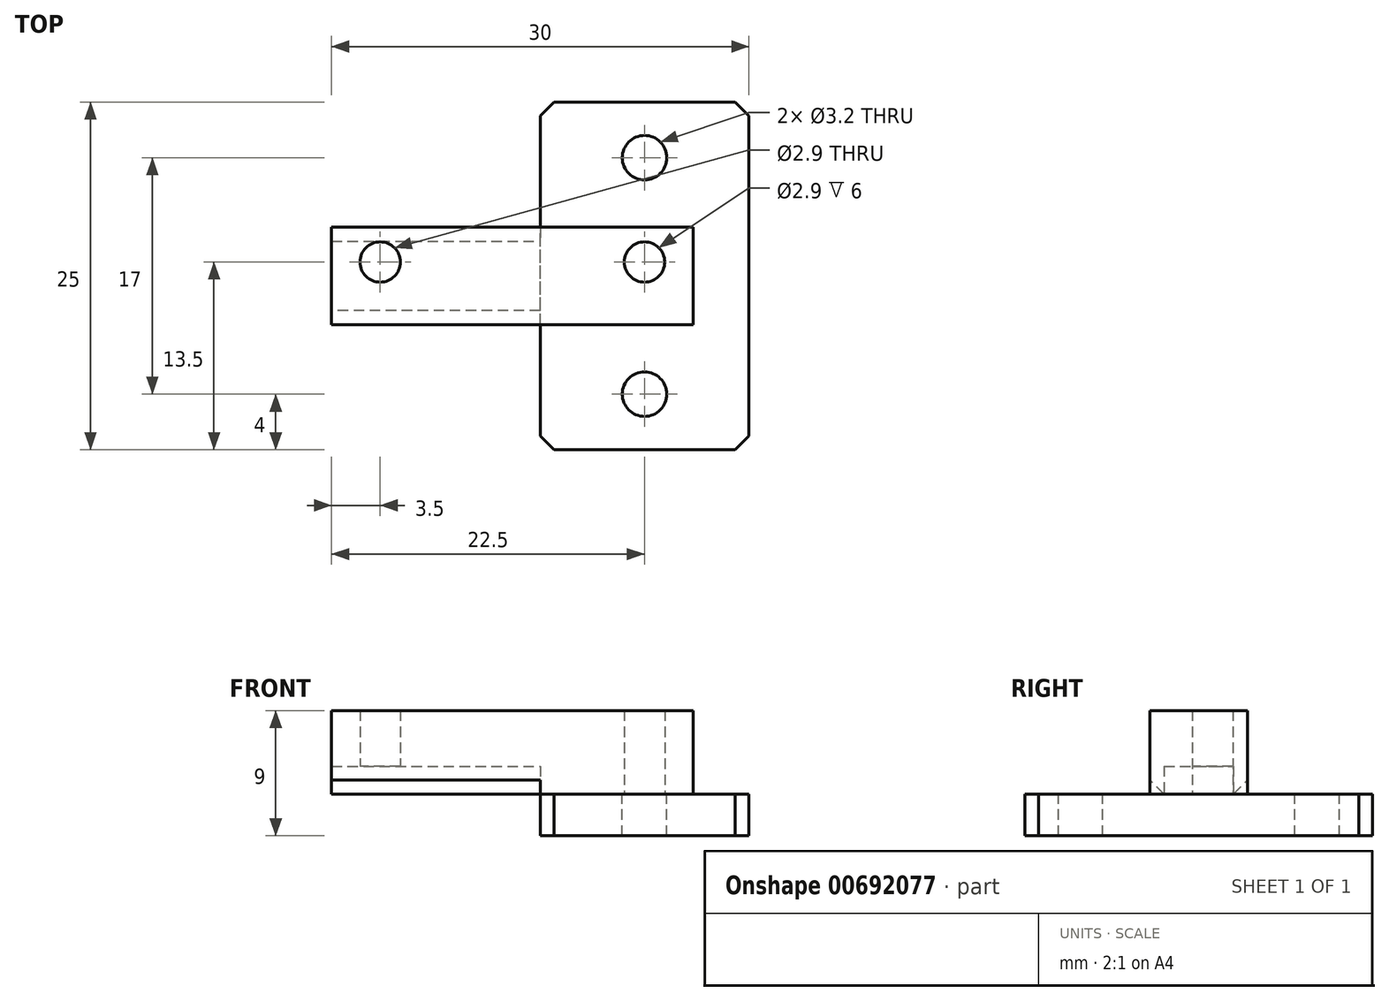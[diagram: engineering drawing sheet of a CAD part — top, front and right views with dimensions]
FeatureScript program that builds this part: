
annotation { "Feature Type Name" : "Feature", "Feature Type Description" : "" }
export const myFeature = defineFeature(function(context is Context, id is Id, definition is map)
    precondition{}
    {
        {
            var Q0;
            Q0=qCreatedBy(makeId("Top.planeOp"),FACE);
            var sketch = newSketch(context, id + "F0", { "sketchPlane" : qUnion([Q0])});
            skLineSegment(sketch, "E0.bottom", {"start": v(0, 0) * mm, "end": v(-26, 0) * mm});
            skLineSegment(sketch, "E0.top", {"start": v(0, 7) * mm, "end": v(-26, 7) * mm});
            skLineSegment(sketch, "E0.left", {"start": v(0, 0) * mm, "end": v(0, 7) * mm});
            skLineSegment(sketch, "E0.right", {"start": v(-26, 0) * mm, "end": v(-26, 7) * mm});
            skCircle(sketch, "E1", {"center": v(-22.5, 4.5) * mm, "radius": 1.45 * mm});
            skCircle(sketch, "E2", {"center": v(-3.5, 4.5) * mm, "radius": 1.45 * mm});
            skSolve(sketch);
        }
        {
            var Q0;
            Q0=makeQuery(id+"F0.imprint","IMPRINT",FACE,{"disambiguationData":[TD([[makeQuery(id+"F0.imprint","IMPRINT",EDGE,{"derivedFrom":sQuery(id+"F0.wireOp",EDGE,"E0.bottom")}),-1.0]])]});
            extrude(context, id + "F1", {"entities" : qUnion([Q0]), "depth" : 6 * mm, "offsetDistance" : 25 * mm});
        }
        {
            var Q0;
            Q0=qCreatedBy(makeId("Top.planeOp"),FACE);
            var sketch = newSketch(context, id + "F2", { "sketchPlane" : qUnion([Q0])});
            skLineSegment(sketch, "E3.bottom", {"start": v(4, -9) * mm, "end": v(-11, -9) * mm});
            skLineSegment(sketch, "E3.top", {"start": v(4, 16) * mm, "end": v(-11, 16) * mm});
            skLineSegment(sketch, "E3.left", {"start": v(4, -9) * mm, "end": v(4, 16) * mm});
            skLineSegment(sketch, "E3.right", {"start": v(-11, -9) * mm, "end": v(-11, 16) * mm});
            skCircle(sketch, "E4", {"center": v(-3.5, -5) * mm, "radius": 1.6 * mm});
            skCircle(sketch, "E5", {"center": v(-3.5, 12) * mm, "radius": 1.6 * mm});
            skLineSegment(sketch, "E6.bottom", {"start": v(-6, -9) * mm, "end": v(-1, -9) * mm});
            skLineSegment(sketch, "E6.top", {"start": v(-6, 16) * mm, "end": v(-1, 16) * mm});
            skLineSegment(sketch, "E6.left", {"start": v(-6, -9) * mm, "end": v(-6, 16) * mm});
            skLineSegment(sketch, "E6.right", {"start": v(-1, -9) * mm, "end": v(-1, 16) * mm});
            skSolve(sketch);
        }
        {
            var Q0;
            Q0 = qSketchRegion(id + "F2", true);
            extrude(context, id + "F3", {"entities" : qUnion([Q0]), "operationType" : NewBodyOperationType.ADD, "oppositeDirection" : true, "depth" : 3 * mm, "offsetDistance" : 25 * mm});
        }
        {
            var Q0;
            Q0=makeQuery(id+"F3.opExtrude","SWEPT_EDGE",EDGE,{"disambiguationData":[OSD([sQuery(id+"F2.wireOp",EDGE,"E3.top"),sQuery(id+"F2.wireOp",EDGE,"E3.left")])]});
            var Q1;
            Q1=makeQuery(id+"F3.opExtrude","SWEPT_EDGE",EDGE,{"disambiguationData":[OSD([sQuery(id+"F2.wireOp",EDGE,"E3.top"),sQuery(id+"F2.wireOp",EDGE,"E3.right")])]});
            var Q2;
            Q2=makeQuery(id+"F3.opExtrude","SWEPT_EDGE",EDGE,{"disambiguationData":[OSD([sQuery(id+"F2.wireOp",EDGE,"E3.bottom"),sQuery(id+"F2.wireOp",EDGE,"E3.left")])]});
            var Q3;
            Q3=makeQuery(id+"F3.opExtrude","SWEPT_EDGE",EDGE,{"disambiguationData":[OSD([sQuery(id+"F2.wireOp",EDGE,"E3.bottom"),sQuery(id+"F2.wireOp",EDGE,"E3.right")])]});
            chamfer(context, id + "F4", {"entities" : qUnion([Q0, Q1, Q2, Q3]), "width" : 1 * mm, "tangentPropagation" : true});
        }
        {
            var Q0;
            {var subQ0=sQuery(id+"F0.wireOp",EDGE,"E0.bottom");var subQ1=makeQuery(id+"F1.opExtrude","SWEPT_FACE",FACE,{"disambiguationData":[OSD([subQ0])]});var subQ2=sQuery(id+"F2.wireOp",EDGE,"E6.right");var subQ3=sQuery(id+"F2.wireOp",EDGE,"E6.left");var subQ4=makeQuery(id+"FKI23qwZDgR0Qfp_1.opExtrude","CAP_FACE",FACE,{"disambiguationData":[OSD([sQuery(id+"F2.wireOp",EDGE,"E4"),sQuery(id+"F2.wireOp",EDGE,"E5"),sQuery(id+"F2.wireOp",EDGE,"E6.bottom"),sQuery(id+"F2.wireOp",EDGE,"E6.top"),subQ3,subQ2])],"isStart":true});var subQ5=makeQuery(id+"F1.opExtrude","CAP_EDGE",EDGE,{"disambiguationData":[OSD([subQ0])],"isStart":true});var subQ6=sQuery(id+"F0.wireOp",EDGE,"E0.right");var subQ7=sQuery(id+"F0.wireOp",EDGE,"E0.left");var subQ8=makeQuery(id+"F1.opExtrude","CAP_FACE",FACE,{"disambiguationData":[OSD([subQ0,sQuery(id+"F0.wireOp",EDGE,"E0.top"),subQ7,subQ6,sQuery(id+"F0.wireOp",EDGE,"E1"),sQuery(id+"F0.wireOp",EDGE,"E2")])],"isStart":true});Q0=makeQuery(id+"F3.boolean.opBoolean","MERGE",EDGE,{"derivedFrom":[makeQuery(id+"FKI23qwZDgR0Qfp_1.boolean.opBoolean","SPLIT",EDGE,{"disambiguationData":[topologyDisambiguationEdgeConnected([subQ1,subQ8]),TD([makeQuery(id+"F1.opExtrude","SWEPT_FACE",FACE,{"disambiguationData":[OSD([subQ7])]})])],"derivedFrom":subQ5}),makeQuery(id+"FKI23qwZDgR0Qfp_1.boolean.opBoolean","SPLIT",EDGE,{"disambiguationData":[topologyDisambiguationEdgeConnected([subQ1,subQ8]),TD([makeQuery(id+"F1.opExtrude","SWEPT_FACE",FACE,{"disambiguationData":[OSD([subQ6])]})])],"derivedFrom":subQ5}),makeQuery(id+"FKI23qwZDgR0Qfp_1.boolean.opBoolean","SPLIT",EDGE,{"disambiguationData":[topologyDisambiguationEdgeConnected([subQ1,subQ4])],"derivedFrom":subQ5})]});}
            var Q1;
            {var subQ0=sQuery(id+"F0.wireOp",EDGE,"E0.top");var subQ1=makeQuery(id+"F1.opExtrude","SWEPT_FACE",FACE,{"disambiguationData":[OSD([subQ0])]});var subQ2=sQuery(id+"F2.wireOp",EDGE,"E6.right");var subQ3=sQuery(id+"F2.wireOp",EDGE,"E6.left");var subQ4=makeQuery(id+"FKI23qwZDgR0Qfp_1.opExtrude","CAP_FACE",FACE,{"disambiguationData":[OSD([sQuery(id+"F2.wireOp",EDGE,"E4"),sQuery(id+"F2.wireOp",EDGE,"E5"),sQuery(id+"F2.wireOp",EDGE,"E6.bottom"),sQuery(id+"F2.wireOp",EDGE,"E6.top"),subQ3,subQ2])],"isStart":true});var subQ5=makeQuery(id+"F1.opExtrude","CAP_EDGE",EDGE,{"disambiguationData":[OSD([subQ0])],"isStart":true});var subQ6=sQuery(id+"F0.wireOp",EDGE,"E0.right");var subQ7=sQuery(id+"F0.wireOp",EDGE,"E0.left");var subQ8=makeQuery(id+"F1.opExtrude","CAP_FACE",FACE,{"disambiguationData":[OSD([sQuery(id+"F0.wireOp",EDGE,"E0.bottom"),subQ0,subQ7,subQ6,sQuery(id+"F0.wireOp",EDGE,"E1"),sQuery(id+"F0.wireOp",EDGE,"E2")])],"isStart":true});Q1=makeQuery(id+"F3.boolean.opBoolean","MERGE",EDGE,{"derivedFrom":[makeQuery(id+"FKI23qwZDgR0Qfp_1.boolean.opBoolean","SPLIT",EDGE,{"disambiguationData":[topologyDisambiguationEdgeConnected([subQ8,subQ1]),TD([makeQuery(id+"F1.opExtrude","SWEPT_FACE",FACE,{"disambiguationData":[OSD([subQ7])]})])],"derivedFrom":subQ5}),makeQuery(id+"FKI23qwZDgR0Qfp_1.boolean.opBoolean","SPLIT",EDGE,{"disambiguationData":[topologyDisambiguationEdgeConnected([subQ8,subQ1]),TD([makeQuery(id+"F1.opExtrude","SWEPT_FACE",FACE,{"disambiguationData":[OSD([subQ6])]})])],"derivedFrom":subQ5}),makeQuery(id+"FKI23qwZDgR0Qfp_1.boolean.opBoolean","SPLIT",EDGE,{"disambiguationData":[topologyDisambiguationEdgeConnected([subQ1,subQ4])],"derivedFrom":subQ5})]});}
            var Q2;
            Q2=makeQuery(id+"F1.opExtrude","CAP_EDGE",EDGE,{"disambiguationData":[OSD([sQuery(id+"F0.wireOp",EDGE,"E0.left")])],"isStart":true});
            chamfer(context, id + "F5", {"entities" : qUnion([Q0, Q1, Q2]), "width" : 1 * mm, "tangentPropagation" : true});
        }
        {
            var Q0;
            {var subQ0=sQuery(id+"F0.wireOp",EDGE,"E1");var subQ2=sQuery(id+"F0.wireOp",EDGE,"E0.top");var subQ3=sQuery(id+"F0.wireOp",EDGE,"E0.right");var subQ4=sQuery(id+"F0.wireOp",EDGE,"E0.bottom");Q0=makeQuery(id+"FKI23qwZDgR0Qfp_1.boolean.opBoolean","SPLIT",FACE,{"disambiguationData":[TD([makeQuery(id+"F1.opExtrude","SWEPT_FACE",FACE,{"disambiguationData":[OSD([subQ3])]})])],"derivedFrom":makeQuery(id+"F1.opExtrude","CAP_FACE",FACE,{"disambiguationData":[OSD([subQ4,subQ2,sQuery(id+"F0.wireOp",EDGE,"E0.left"),subQ3,subQ0,sQuery(id+"F0.wireOp",EDGE,"E2")])],"isStart":true})});}
            extrude(context, id + "F6", {"entities" : qUnion([Q0]), "operationType" : NewBodyOperationType.REMOVE, "oppositeDirection" : true, "depth" : 2 * mm, "offsetDistance" : 25 * mm});
        }
    });
